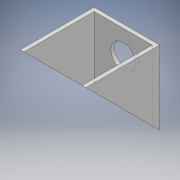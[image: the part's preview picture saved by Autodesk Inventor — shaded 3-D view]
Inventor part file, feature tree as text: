
AUTODESK INVENTOR PART (.ipt)
format: ipt  version: 2018 (Build 220112000, 112)  size: 114,176 bytes
history: native  units: mm
features: sketch x3, extrude x2, other x1, chamfer x1, hole x1
ambient origin geometry x8: Origin, YZ Plane, XZ Plane, XY Plane, X Axis, Y Axis, Z Axis, Center Point
bodies: Body1 (feature_tree)
feature tree (8):
  other  "ソリッド1"
  extrude  "押し出し1"  Depth=40.0mm
  chamfer  "面取り1"  Distance=60.0mm
  hole  "穴1"  [1 undecoded]
  extrude  "押し出し2"  Depth=60.0mm TaperAngle=0.0deg
  sketch  "スケッチ1"
  sketch  "スケッチ2"
  sketch  "スケッチ4"
note: 1 required parameter value undecoded (feature->parameter linkage not recoverable at this tier; creation-order binding heuristic only, values carry confidence <= 0.55)
